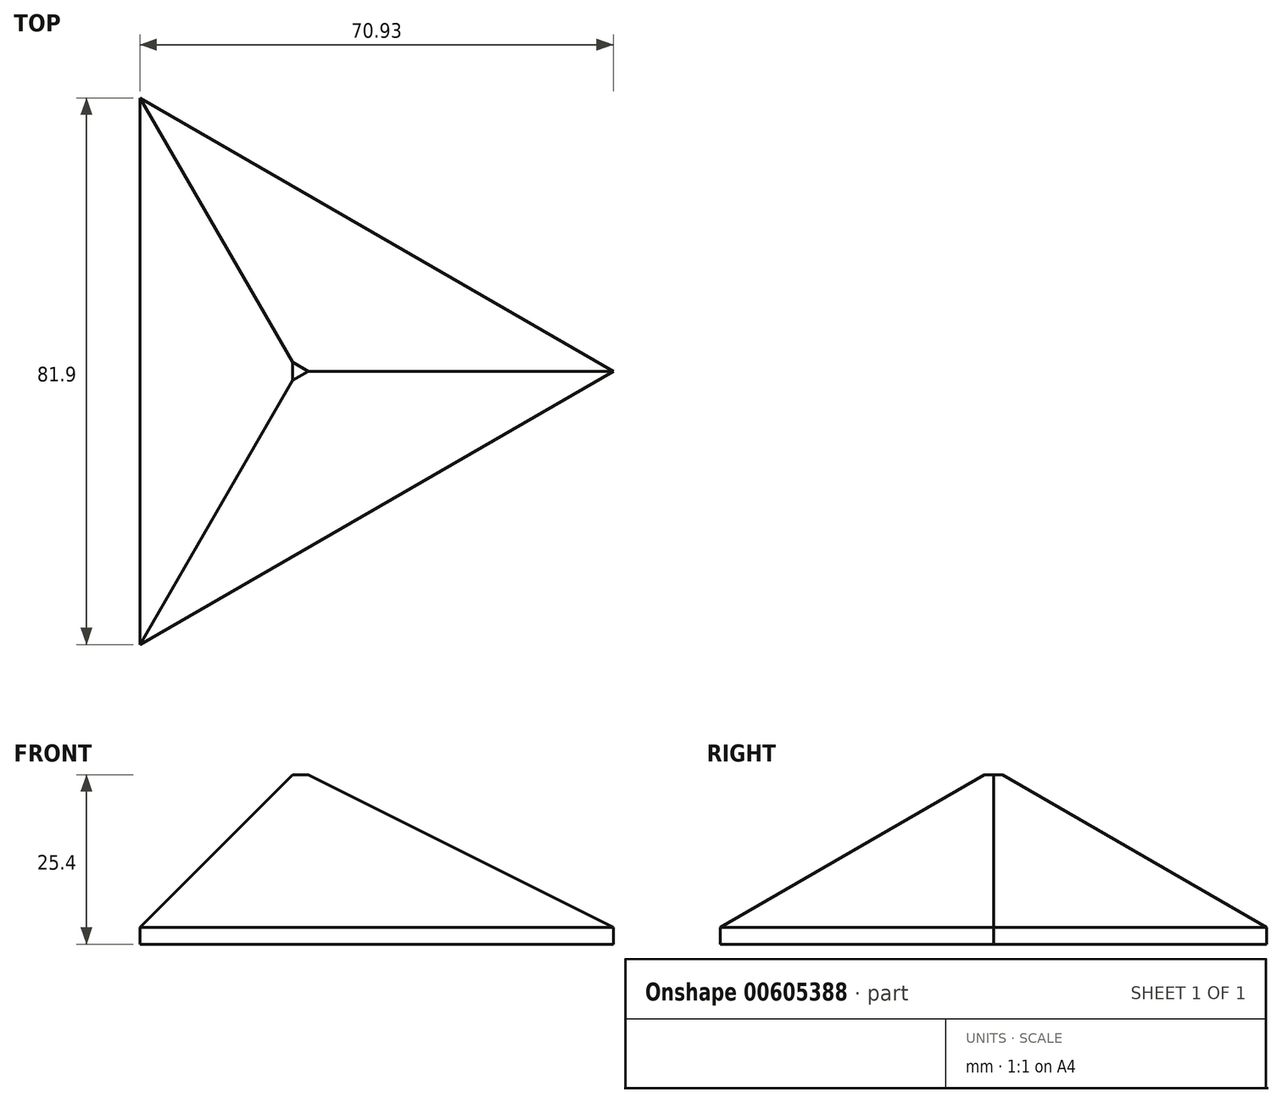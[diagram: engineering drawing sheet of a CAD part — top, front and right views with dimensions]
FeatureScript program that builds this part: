
annotation { "Feature Type Name" : "Feature", "Feature Type Description" : "" }
export const myFeature = defineFeature(function(context is Context, id is Id, definition is map)
    precondition{}
    {
        {
            var Q0;
            Q0=qCreatedBy(makeId("Top.planeOp"),FACE);
            var sketch = newSketch(context, id + "F0", { "sketchPlane" : qUnion([Q0])});
            skCircle(sketch, "E0.cCircle", {"center": v(0, 0) * mm, "radius": 47.29 * mm, "construction": true});
            skLineSegment(sketch, "E0.0", {"start": v(47.29, 0) * mm, "end": v(-23.64, -40.95) * mm});
            skLineSegment(sketch, "E0.1", {"start": v(-23.64, -40.95) * mm, "end": v(-23.64, 40.95) * mm});
            skLineSegment(sketch, "E0.2", {"start": v(-23.64, 40.95) * mm, "end": v(47.29, 0) * mm});
            skSolve(sketch);
        }
        {
            var Q0;
            Q0=makeQuery(id+"F0.imprint","IMPRINT",FACE,{"disambiguationData":[TD([[makeQuery(id+"F0.imprint","IMPRINT",EDGE,{"derivedFrom":sQuery(id+"F0.wireOp",EDGE,"E0.0")}),-1.0]])]});
            extrude(context, id + "F1", {"entities" : qUnion([Q0]), "depth" : 25.4 * mm, "offsetDistance" : 25.4 * mm});
        }
        {
            var Q0;
            Q0=makeQuery(id+"F1.opExtrude","CAP_EDGE",EDGE,{"disambiguationData":[OSD([sQuery(id+"F0.wireOp",EDGE,"E0.0")])],"isStart":false});
            var Q1;
            Q1=makeQuery(id+"F1.opExtrude","CAP_EDGE",EDGE,{"disambiguationData":[OSD([sQuery(id+"F0.wireOp",EDGE,"E0.2")])],"isStart":false});
            var Q2;
            Q2=makeQuery(id+"F1.opExtrude","CAP_FACE",FACE,{"disambiguationData":[OSD([sQuery(id+"F0.wireOp",EDGE,"E0.0"),sQuery(id+"F0.wireOp",EDGE,"E0.1"),sQuery(id+"F0.wireOp",EDGE,"E0.2")])],"isStart":false});
            chamfer(context, id + "F2", {"entities" : qUnion([Q0, Q1, Q2]), "width" : 22.86 * mm, "tangentPropagation" : true});
        }
    });
